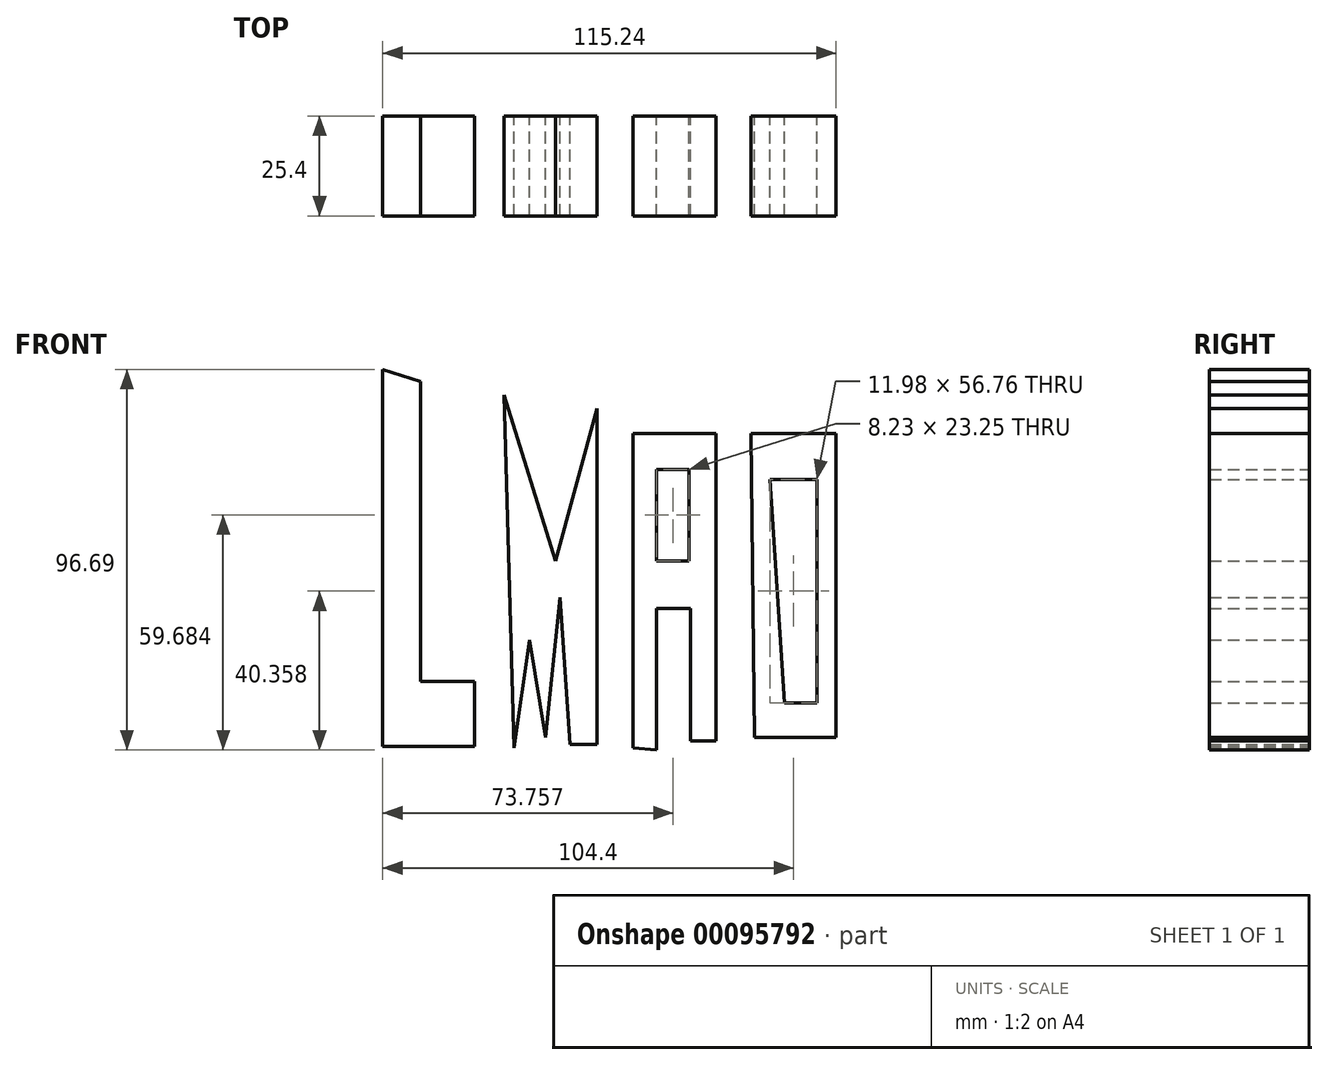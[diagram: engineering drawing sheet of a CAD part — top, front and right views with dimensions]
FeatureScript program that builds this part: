
annotation { "Feature Type Name" : "Feature", "Feature Type Description" : "" }
export const myFeature = defineFeature(function(context is Context, id is Id, definition is map)
    precondition{}
    {
        {
            var Q0;
            Q0=qCreatedBy(makeId("Front.planeOp"),FACE);
            var sketch = newSketch(context, id + "F0", { "sketchPlane" : qUnion([Q0])});
            skLineSegment(sketch, "E0", {"start": v(-69.64, 48.63) * mm, "end": v(-69.64, -47.2) * mm});
            skLineSegment(sketch, "E1", {"start": v(-69.64, -47.2) * mm, "end": v(-46.25, -47.2) * mm});
            skLineSegment(sketch, "E2", {"start": v(-46.25, -47.2) * mm, "end": v(-46.25, -30.66) * mm});
            skLineSegment(sketch, "E3", {"start": v(-46.25, -30.66) * mm, "end": v(-59.94, -30.66) * mm});
            skLineSegment(sketch, "E4", {"start": v(-59.94, -30.66) * mm, "end": v(-59.94, 45.5) * mm});
            skLineSegment(sketch, "E5", {"start": v(-59.94, 45.5) * mm, "end": v(-69.64, 48.63) * mm});
            skLineSegment(sketch, "E6", {"start": v(-36.26, -47.5) * mm, "end": v(-38.83, 42.07) * mm});
            skLineSegment(sketch, "E7", {"start": v(-38.83, 42.07) * mm, "end": v(-25.71, 0) * mm});
            skLineSegment(sketch, "E8", {"start": v(-25.71, 0) * mm, "end": v(-15.16, 38.65) * mm});
            skLineSegment(sketch, "E9", {"start": v(-15.16, 38.65) * mm, "end": v(-15.16, -46.64) * mm});
            skLineSegment(sketch, "E10", {"start": v(-15.16, -46.64) * mm, "end": v(-22, -46.64) * mm});
            skLineSegment(sketch, "E11", {"start": v(-22, -46.64) * mm, "end": v(-24.57, -9.27) * mm});
            skLineSegment(sketch, "E12", {"start": v(-24.57, -9.27) * mm, "end": v(-28.28, -44.93) * mm});
            skLineSegment(sketch, "E13", {"start": v(-28.28, -44.93) * mm, "end": v(-32.27, -20.1) * mm});
            skLineSegment(sketch, "E14", {"start": v(-32.27, -20.1) * mm, "end": v(-36.26, -47.5) * mm});
            skLineSegment(sketch, "E15", {"start": v(-6.03, 32.37) * mm, "end": v(-6.03, -47.5) * mm});
            skLineSegment(sketch, "E16", {"start": v(-6.03, -47.5) * mm, "end": v(-6.03, 32.37) * mm});
            skLineSegment(sketch, "E17", {"start": v(-6.03, 32.37) * mm, "end": v(15.08, 32.37) * mm});
            skLineSegment(sketch, "E18", {"start": v(15.08, -45.78) * mm, "end": v(15.08, 32.37) * mm});
            skLineSegment(sketch, "E19", {"start": v(15.08, -45.78) * mm, "end": v(8.52, -45.78) * mm});
            skLineSegment(sketch, "E20", {"start": v(8.52, -45.78) * mm, "end": v(8.52, -12.12) * mm});
            skLineSegment(sketch, "E21", {"start": v(8.52, -12.12) * mm, "end": v(0, -12.12) * mm});
            skLineSegment(sketch, "E22", {"start": v(0, -12.12) * mm, "end": v(0, -48.06) * mm});
            skLineSegment(sketch, "E23", {"start": v(0, -48.06) * mm, "end": v(-6.03, -47.5) * mm});
            skLineSegment(sketch, "E24", {"start": v(23.92, 32.37) * mm, "end": v(45.6, 32.37) * mm});
            skLineSegment(sketch, "E25", {"start": v(45.6, 32.37) * mm, "end": v(45.6, -44.93) * mm});
            skLineSegment(sketch, "E26", {"start": v(45.6, -44.93) * mm, "end": v(24.78, -44.93) * mm});
            skLineSegment(sketch, "E27", {"start": v(24.78, -44.93) * mm, "end": v(23.92, 32.37) * mm});
            skLineSegment(sketch, "E28", {"start": v(28.77, 20.68) * mm, "end": v(40.75, 20.68) * mm});
            skLineSegment(sketch, "E29", {"start": v(40.75, 20.68) * mm, "end": v(40.75, -36.08) * mm});
            skLineSegment(sketch, "E30", {"start": v(40.75, -36.08) * mm, "end": v(32.48, -36.08) * mm});
            skLineSegment(sketch, "E31", {"start": v(32.48, -36.08) * mm, "end": v(28.77, 20.68) * mm});
            skLineSegment(sketch, "E32", {"start": v(0, 23.25) * mm, "end": v(8.23, 23.25) * mm});
            skLineSegment(sketch, "E33", {"start": v(8.23, 23.25) * mm, "end": v(8.23, 0) * mm});
            skLineSegment(sketch, "E34", {"start": v(8.23, 0) * mm, "end": v(0, 0) * mm});
            skLineSegment(sketch, "E35", {"start": v(0, 0) * mm, "end": v(0, 23.25) * mm});
            skSolve(sketch);
        }
        {
            var Q0;
            Q0 = qSketchRegion(id + "F0", true);
            extrude(context, id + "F1", {"entities" : qUnion([Q0]), "depth" : 25.4 * mm});
        }
    });
